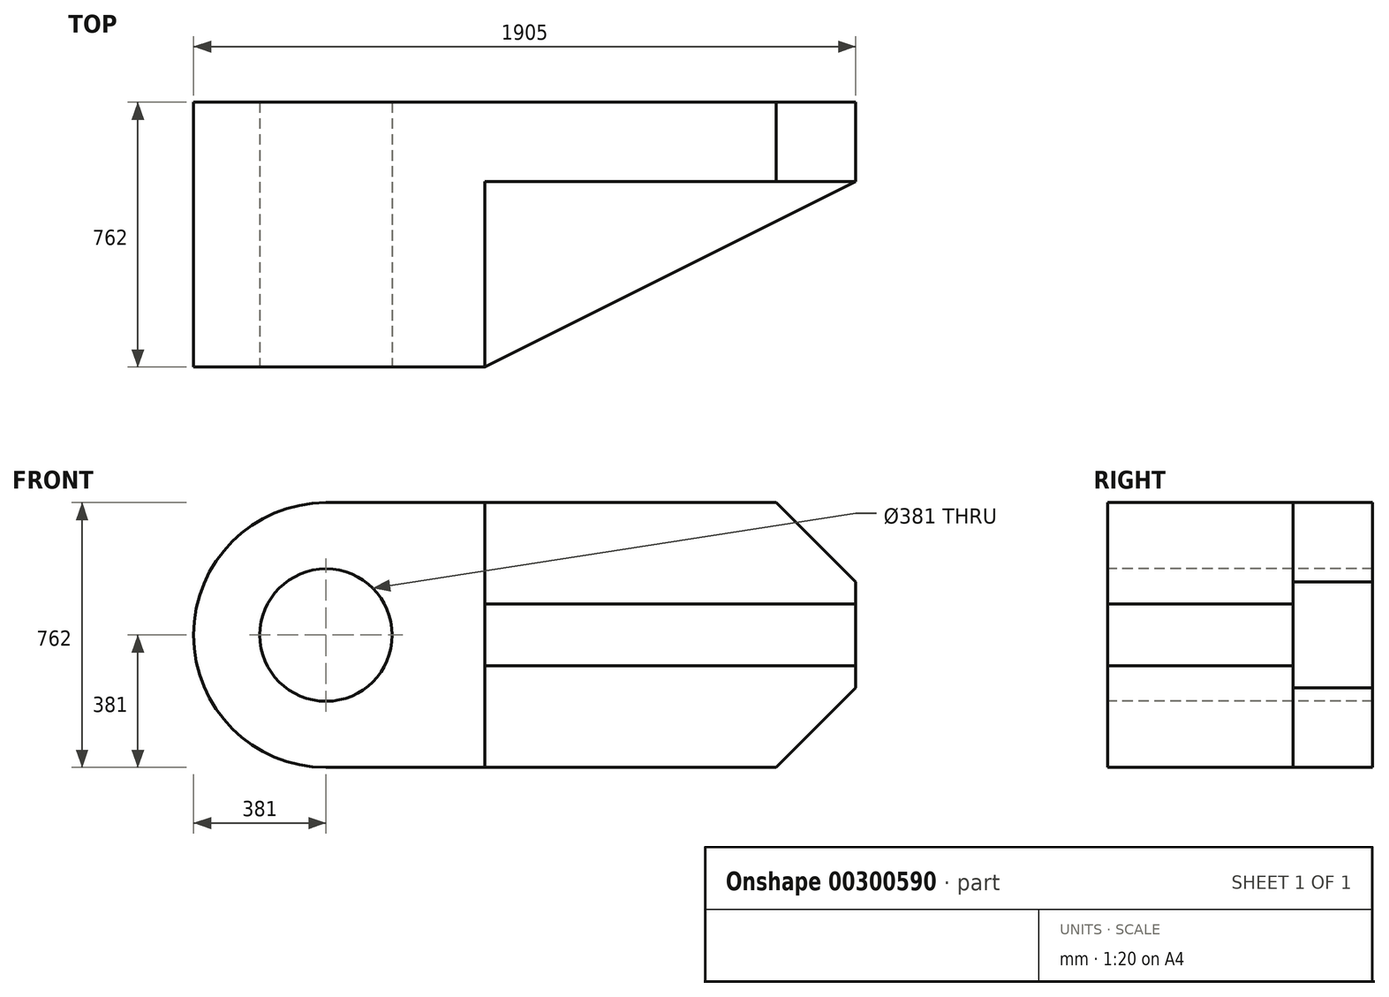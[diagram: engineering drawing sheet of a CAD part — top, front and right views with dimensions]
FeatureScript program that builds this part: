
annotation { "Feature Type Name" : "Feature", "Feature Type Description" : "" }
export const myFeature = defineFeature(function(context is Context, id is Id, definition is map)
    precondition{}
    {
        {
            var Q0;
            Q0=qCreatedBy(makeId("Front.planeOp"),FACE);
            var sketch = newSketch(context, id + "F0", { "sketchPlane" : qUnion([Q0])});
            skArc(sketch, "E0", {"start": v(0, 762) * mm, "mid": v(-381, 381) * mm, "end": v(0, 0) * mm});
            skLineSegment(sketch, "E1", {"start": v(0, 0) * mm, "end": v(1524, 0) * mm});
            skLineSegment(sketch, "E2", {"start": v(0, 762) * mm, "end": v(1524, 762) * mm});
            skLineSegment(sketch, "E3", {"start": v(1524, 762) * mm, "end": v(1524, 0) * mm});
            skSolve(sketch);
        }
        {
            var Q0;
            Q0=makeQuery(id+"F0.imprint","IMPRINT",FACE,{"disambiguationData":[TD([[makeQuery(id+"F0.imprint","IMPRINT",EDGE,{"derivedFrom":sQuery(id+"F0.wireOp",EDGE,"E0")}),1.0]])]});
            extrude(context, id + "F1", {"entities" : qUnion([Q0]), "depth" : 762 * mm});
        }
        {
            var Q0;
            Q0=makeQuery(id+"F1.opExtrude","CAP_FACE",FACE,{"disambiguationData":[OSD([sQuery(id+"F0.wireOp",EDGE,"E0"),sQuery(id+"F0.wireOp",EDGE,"E1"),sQuery(id+"F0.wireOp",EDGE,"E2"),sQuery(id+"F0.wireOp",EDGE,"E3")])],"isStart":false});
            var sketch = newSketch(context, id + "F2", { "sketchPlane" : qUnion([Q0])});
            skLineSegment(sketch, "E4", {"start": v(457.2, 762) * mm, "end": v(1524, 762) * mm});
            skLineSegment(sketch, "E5", {"start": v(1524, 762) * mm, "end": v(1524, 0) * mm});
            skLineSegment(sketch, "E6", {"start": v(1524, 0) * mm, "end": v(457.2, 0) * mm});
            skLineSegment(sketch, "E7", {"start": v(457.2, 762) * mm, "end": v(457.2, 0) * mm});
            skSolve(sketch);
        }
        {
            var Q0;
            Q0=makeQuery(id+"F2.imprint","IMPRINT",FACE,{"disambiguationData":[TD([[makeQuery(id+"F2.imprint","IMPRINT",EDGE,{"derivedFrom":sQuery(id+"F2.wireOp",EDGE,"E4")}),-1.0]])]});
            extrude(context, id + "F3", {"entities" : qUnion([Q0]), "operationType" : NewBodyOperationType.REMOVE, "oppositeDirection" : true, "depth" : 533.4 * mm});
        }
        {
            var Q0;
            Q0=makeQuery(id+"F3.boolean.opBoolean","COPY",FACE,{"derivedFrom":makeQuery(id+"F3.opExtrude","CAP_FACE",FACE,{"disambiguationData":[OSD([sQuery(id+"F2.wireOp",EDGE,"E4"),sQuery(id+"F2.wireOp",EDGE,"E5"),sQuery(id+"F2.wireOp",EDGE,"E6"),sQuery(id+"F2.wireOp",EDGE,"E7")])],"isStart":false})});
            var sketch = newSketch(context, id + "F4", { "sketchPlane" : qUnion([Q0])});
            skLineSegment(sketch, "E8", {"start": v(1524, 0) * mm, "end": v(1524, 228.6) * mm});
            skLineSegment(sketch, "E9", {"start": v(1524, 762) * mm, "end": v(1524, 533.4) * mm});
            skLineSegment(sketch, "E10", {"start": v(1524, 533.4) * mm, "end": v(1295.4, 762) * mm});
            skLineSegment(sketch, "E11", {"start": v(1295.4, 0) * mm, "end": v(1524, 228.6) * mm});
            skLineSegment(sketch, "E12", {"start": v(1524, 0) * mm, "end": v(1295.4, 0) * mm});
            skSolve(sketch);
        }
        {
            var Q0;
            Q0 = qSketchRegion(id + "F4", true);
            var Q1;
            {var subQ0=sQuery(id+"F4.wireOp",EDGE,"E10");Q1=makeQuery(id+"F4.imprint","IMPRINT",FACE,{"disambiguationData":[TD([[makeQuery(id+"F4.imprint","IMPRINT",EDGE,{"derivedFrom":subQ0}),-1.0]])]});}
            extrude(context, id + "F5", {"entities" : qUnion([Q0, Q1]), "operationType" : NewBodyOperationType.REMOVE, "oppositeDirection" : true, "depth" : 228.6 * mm});
        }
        {
            var Q0;
            Q0=makeQuery(id+"F3.boolean.opBoolean","COPY",FACE,{"derivedFrom":makeQuery(id+"F3.opExtrude","CAP_FACE",FACE,{"disambiguationData":[OSD([sQuery(id+"F2.wireOp",EDGE,"E4"),sQuery(id+"F2.wireOp",EDGE,"E5"),sQuery(id+"F2.wireOp",EDGE,"E6"),sQuery(id+"F2.wireOp",EDGE,"E7")])],"isStart":false})});
            var sketch = newSketch(context, id + "F6", { "sketchPlane" : qUnion([Q0])});
            skLineSegment(sketch, "E13", {"start": v(1524, 228.6) * mm, "end": v(1524, 292.1) * mm});
            skLineSegment(sketch, "E14", {"start": v(1524, 533.4) * mm, "end": v(1524, 469.9) * mm});
            skLineSegment(sketch, "E15", {"start": v(1524, 292.1) * mm, "end": v(457.2, 292.1) * mm});
            skLineSegment(sketch, "E16", {"start": v(1524, 469.9) * mm, "end": v(457.2, 469.9) * mm});
            skLineSegment(sketch, "E17", {"start": v(457.2, 292.1) * mm, "end": v(457.2, 469.9) * mm});
            skLineSegment(sketch, "E18", {"start": v(1524, 292.1) * mm, "end": v(1524, 469.9) * mm});
            skSolve(sketch);
        }
        {
            var Q0;
            Q0=makeQuery(id+"F6.imprint","IMPRINT",FACE,{"disambiguationData":[TD([[makeQuery(id+"F6.imprint","IMPRINT",EDGE,{"derivedFrom":sQuery(id+"F6.wireOp",EDGE,"E15")}),-1.0]])]});
            extrude(context, id + "F7", {"entities" : qUnion([Q0]), "operationType" : NewBodyOperationType.ADD, "depth" : 533.4 * mm});
        }
        {
            var Q0;
            Q0=makeQuery(id+"F7.opExtrude","SWEPT_FACE",FACE,{"disambiguationData":[OSD([sQuery(id+"F6.wireOp",EDGE,"E15")])]});
            var sketch = newSketch(context, id + "F8", { "sketchPlane" : qUnion([Q0])});
            skLineSegment(sketch, "E19", {"start": v(457.2, 762) * mm, "end": v(1524, 228.6) * mm});
            skLineSegment(sketch, "E20", {"start": v(1524, 228.6) * mm, "end": v(457.2, 228.6) * mm});
            skLineSegment(sketch, "E21", {"start": v(457.2, 228.6) * mm, "end": v(457.2, 762) * mm});
            skSolve(sketch);
        }
        {
            var Q0;
            Q0=makeQuery(id+"F8.imprint","IMPRINT",FACE,{"disambiguationData":[TD([[makeQuery(id+"F8.imprint","IMPRINT",EDGE,{"derivedFrom":sQuery(id+"F8.wireOp",EDGE,"E19")}),1.0]])]});
            extrude(context, id + "F9", {"entities" : qUnion([Q0]), "operationType" : NewBodyOperationType.REMOVE, "oppositeDirection" : true, "depth" : 254 * mm});
        }
        {
            var Q0;
            Q0=makeQuery(id+"F7.boolean.opBoolean","MERGE",FACE,{"derivedFrom":[makeQuery(id+"F1.opExtrude","CAP_FACE",FACE,{"disambiguationData":[OSD([sQuery(id+"F0.wireOp",EDGE,"E0"),sQuery(id+"F0.wireOp",EDGE,"E1"),sQuery(id+"F0.wireOp",EDGE,"E2"),sQuery(id+"F0.wireOp",EDGE,"E3")])],"isStart":false}),makeQuery(id+"F7.opExtrude","CAP_FACE",FACE,{"disambiguationData":[OSD([sQuery(id+"F6.wireOp",EDGE,"E15"),sQuery(id+"F6.wireOp",EDGE,"E16"),sQuery(id+"F6.wireOp",EDGE,"E17"),sQuery(id+"F6.wireOp",EDGE,"E18")])],"isStart":false})]});
            var sketch = newSketch(context, id + "F10", { "sketchPlane" : qUnion([Q0])});
            skCircle(sketch, "E22", {"center": v(0, 381) * mm, "radius": 190.5 * mm});
            skSolve(sketch);
        }
        {
            var Q0;
            Q0 = qSketchRegion(id + "F10", true);
            extrude(context, id + "F11", {"entities" : qUnion([Q0]), "operationType" : NewBodyOperationType.REMOVE, "oppositeDirection" : true, "depth" : 762 * mm});
        }
    });
